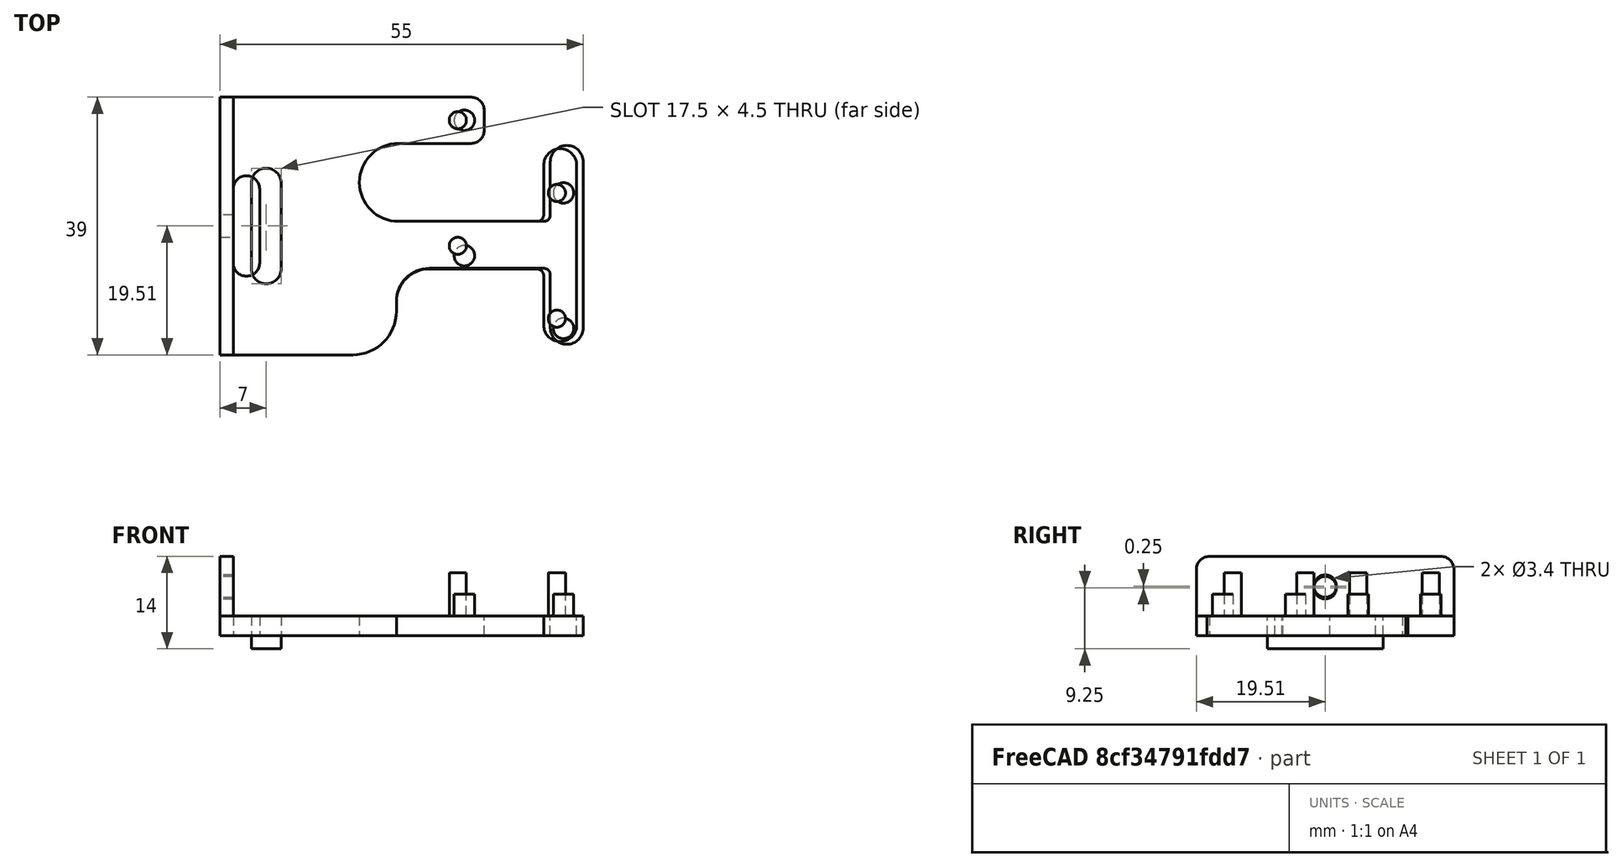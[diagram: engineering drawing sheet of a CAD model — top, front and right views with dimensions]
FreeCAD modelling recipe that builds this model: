
FCSTD DOCUMENT  (FreeCAD 0.15R4649 (Git))
Label: renacuajo-snifferV3
License: CC-BY 3.0
LicenseURL: http://creativecommons.org/licenses/by/3.0/
objects: Sketcher::SketchObject×5, PartDesign::Pad×3, PartDesign::Pocket×2, Part::Feature×1, Part::MultiFuse×1, Mesh::Feature×1, Part::Fillet×1
note: 18 computed .brp shape members not serialized (recipe doc carries the construction recipe); baked Part::Feature solids carry a one-line shape summary decoded from their .brp

FEATURE [Sketcher::SketchObject] Sketch  label="sniffer-base-sketch"
  sketch-geometry (20):
    g0: LineSegment StartX=-27 StartY=-19.5085 StartZ=0 EndX=-27 EndY=19.4915 EndZ=0
    g1: LineSegment StartX=-27 StartY=19.4915 StartZ=0 EndX=11 EndY=19.4915 EndZ=0
    g2: LineSegment StartX=13 StartY=17.4915 StartZ=0 EndX=13 EndY=14.4915 EndZ=0
    g3: LineSegment StartX=11 StartY=12.4915 StartZ=0 EndX=0 EndY=12.4915 EndZ=0
    g4: LineSegment StartX=-27 StartY=-19.5085 StartZ=0 EndX=-6.9 EndY=-19.5085 EndZ=0
    g5: LineSegment StartX=-0.3 StartY=-12.9085 StartZ=0 EndX=-0.3 EndY=-11.4085 EndZ=0
    g6: LineSegment StartX=4.7 StartY=-6.4085 StartZ=0 EndX=22 EndY=-6.4085 EndZ=0
    g7: LineSegment StartX=23 StartY=-7.4085 StartZ=0 EndX=23 EndY=-15.4085 EndZ=0
    g8: LineSegment StartX=28 StartY=-15.4085 StartZ=0 EndX=28 EndY=9.6915 EndZ=0
    g9: LineSegment StartX=23 StartY=9.69149 StartZ=0 EndX=23 EndY=1.69149 EndZ=0
    g10: LineSegment StartX=22 StartY=0.691495 StartZ=0 EndX=-3.5568e-08 EndY=0.691495 EndZ=0
    g11: ArcOfCircle CenterX=-9.4139e-08 CenterY=6.5915 CenterZ=0 NormalX=0 NormalY=0 NormalZ=1 Radius=5.9 StartAngle=1.5708 EndAngle=4.71239
    g12: ArcOfCircle CenterX=11 CenterY=17.4915 CenterZ=0 NormalX=0 NormalY=0 NormalZ=1 Radius=2 StartAngle=0 EndAngle=1.5708
    g13: ArcOfCircle CenterX=11 CenterY=14.4915 CenterZ=0 NormalX=0 NormalY=0 NormalZ=1 Radius=2 StartAngle=4.71239 EndAngle=6.28319
    g14: ArcOfCircle CenterX=-6.9 CenterY=-12.9085 CenterZ=0 NormalX=0 NormalY=0 NormalZ=1 Radius=6.6 StartAngle=4.71239 EndAngle=6.28319
    g15: ArcOfCircle CenterX=4.7 CenterY=-11.4085 CenterZ=0 NormalX=0 NormalY=0 NormalZ=1 Radius=5 StartAngle=1.5708 EndAngle=3.14159
    g16: ArcOfCircle CenterX=22 CenterY=-7.4085 CenterZ=0 NormalX=0 NormalY=0 NormalZ=1 Radius=1 StartAngle=0 EndAngle=1.5708
    g17: ArcOfCircle CenterX=25.5 CenterY=-15.4085 CenterZ=0 NormalX=0 NormalY=0 NormalZ=1 Radius=2.5 StartAngle=3.1416 EndAngle=6.28319
    g18: ArcOfCircle CenterX=22 CenterY=1.69149 CenterZ=0 NormalX=0 NormalY=0 NormalZ=1 Radius=1 StartAngle=4.71239 EndAngle=6.28319
    g19: ArcOfCircle CenterX=25.5 CenterY=9.6915 CenterZ=0 NormalX=0 NormalY=0 NormalZ=1 Radius=2.5 StartAngle=1.3074e-08 EndAngle=3.14159
  constraints (57):
    c: Vertical(g0)
    c: Coincident(g0,g1)
    c: Horizontal(g1)
    c: Vertical(g2)
    c: Horizontal(g3)
    c: Horizontal(g4)
    c: Horizontal(g6)
    c: Vertical(g7)
    c: Vertical(g8)
    c: Vertical(g9)
    c: Horizontal(g10)
    c: Coincident(g4,g0)
    c: Vertical(g5)
    c: PointOnObject(g11,g-2)
    c: Coincident(g11,g3)
    c: Coincident(g11,g10)
    c: Tangent(g11,g3)
    c: Tangent(g10,g11)
    c: Tangent(g1,g12)
    c: Tangent(g2,g12)
    c: Tangent(g2,g13)
    c: Tangent(g3,g13)
    c: Radius(g12) = 2
    c: Equal(g13,g12)
    c: DistanceY(g1,g3) = -7
    c: DistanceX(g0,g2) = 40
    c: DistanceY(g0) = 39
    c: DistanceY(g3,g10) = -11.8
    c: DistanceX(g0) = -27
    c: DistanceY(g0) = 19.4915
    c: Tangent(g4,g14)
    c: Tangent(g5,g14)
    c: Tangent(g5,g15)
    c: Tangent(g6,g15)
    c: DistanceX(g0,g5) = 26.7
    c: Radius(g14) = 6.6
    c: Radius(g15) = 5
    c: DistanceY(g5) = 1.5
    c: Tangent(g6,g16)
    c: Tangent(g7,g16)
    c: DistanceX(g7,g5) = -23.3
    c: Radius(g16) = 1
    c: Coincident(g17,g7)
    c: Coincident(g17,g8)
    c: Tangent(g7,g17)
    c: Tangent(g17,g8)
    c: DistanceY(g7) = -8
    c: Tangent(g9,g18)
    c: Tangent(g10,g18)
    c: Equal(g16,g18)
    c: Equal(g7,g9)
    c: Coincident(g19,g8)
    c: Coincident(g19,g9)
    c: Tangent(g19,g8)
    c: Tangent(g19,g9)
    c: Equal(g19,g17)
    c: DistanceX(g7,g8) = 5
FEATURE [PartDesign::Pad] Pad  label="sniffer-base"
  Length = 3
  Length2 = 100
  Sketch = -> Sketch
  Type = 0
FEATURE [Sketcher::SketchObject] Sketch001  label="vertical-wall-sketch"
  ExternalGeometry = -> [Pad]
  Placement = pos=(-27,0,0) rot=(0.57735,-0.57735,-0.57735;2.0944rad)
  Support = -> Pad [Face2]
  sketch-geometry (6):
    g0: LineSegment StartX=-17.4915 StartY=12 StartZ=0 EndX=17.5085 EndY=12 EndZ=0
    g1: LineSegment StartX=19.5085 StartY=10 StartZ=0 EndX=19.5085 EndY=0 EndZ=0
    g2: LineSegment StartX=19.5085 StartY=0 StartZ=0 EndX=-19.4915 EndY=0 EndZ=0
    g3: LineSegment StartX=-19.4915 StartY=0 StartZ=0 EndX=-19.4915 EndY=10 EndZ=0
    g4: ArcOfCircle CenterX=-17.4915 CenterY=10 CenterZ=0 NormalX=0 NormalY=0 NormalZ=1 Radius=2 StartAngle=1.5708 EndAngle=3.14159
    g5: ArcOfCircle CenterX=17.5085 CenterY=10 CenterZ=0 NormalX=0 NormalY=0 NormalZ=1 Radius=2 StartAngle=0 EndAngle=1.5708
  constraints (15):
    c: Coincident(g1,g2)
    c: Coincident(g2,g3)
    c: Horizontal(g0)
    c: Horizontal(g2)
    c: Vertical(g1)
    c: Vertical(g3)
    c: Coincident(g2,g-3)
    c: Coincident(g1,g-3)
    c: Tangent(g0,g4)
    c: Tangent(g3,g4)
    c: Tangent(g0,g5)
    c: Tangent(g1,g5)
    c: DistanceY(g2,g0) = 12
    c: Radius(g4) = 2
    c: Equal(g5,g4)
FEATURE [PartDesign::Pad] Pad001  label="vertical-wall"
  Length = 2
  Length2 = 100
  Reversed = true
  Sketch = -> Sketch001
  Type = 0
FEATURE [Sketcher::SketchObject] Sketch003  label="poles-sketch"
  Placement = pos=(0,0,3) rot=(0,0,1;0rad)
  sketch-geometry (9):
    g0: Circle CenterX=10 CenterY=16 CenterZ=0 NormalX=0 NormalY=0 NormalZ=1 Radius=1.55
    g1: Circle CenterX=25 CenterY=5 CenterZ=0 NormalX=0 NormalY=0 NormalZ=1 Radius=1.55
    g2: Circle CenterX=10 CenterY=-4.5 CenterZ=0 NormalX=0 NormalY=0 NormalZ=1 Radius=1.55
    g3: Circle CenterX=25 CenterY=-15.5 CenterZ=0 NormalX=0 NormalY=0 NormalZ=1 Radius=1.55
    g4: LineSegment [constr] StartX=10 StartY=16 StartZ=0 EndX=10 EndY=-4.5 EndZ=0
    g5: LineSegment [constr] StartX=10 StartY=16 StartZ=0 EndX=25 EndY=16 EndZ=0
    g6: LineSegment [constr] StartX=25 StartY=16 StartZ=0 EndX=25 EndY=5 EndZ=0
    g7: LineSegment [constr] StartX=10 StartY=-4.5 StartZ=0 EndX=25 EndY=-4.5 EndZ=0
    g8: LineSegment [constr] StartX=25 StartY=-4.5 StartZ=0 EndX=25 EndY=-15.5 EndZ=0
  constraints (24):
    c: Radius(g0) = 1.55
    c: Equal(g0,g1)
    c: Equal(g1,g2)
    c: Equal(g2,g3)
    c: DistanceX(g0,g1) = 15
    c: DistanceY(g0,g1) = -11
    c: Vertical(g4)
    c: Coincident(g4,g0)
    c: Coincident(g4,g2)
    c: DistanceX(g0) = 10
    c: DistanceY(g0) = 16
    c: Horizontal(g5)
    c: Vertical(g6)
    c: Coincident(g6,g5)
    c: Coincident(g5,g0)
    c: Coincident(g6,g1)
    c: Horizontal(g7)
    c: Vertical(g8)
    c: Coincident(g7,g8)
    c: Coincident(g7,g2)
    c: DistanceY(g4) = -20.5
    c: Equal(g7,g5)
    c: Equal(g8,g6)
    c: Coincident(g3,g8)
FEATURE [PartDesign::Pad] Pad002  label="poles"
  Length = 3.25
  Length2 = 100
  Placement = pos=(0,0,3) rot=(0,0,1;0rad)
  Sketch = -> Sketch003
  Type = 0
FEATURE [Part::Feature] Pocket001001  label="renacuajo-sniffer"
  shape: bbox 54 x 39 x 12 mm, 38 faces (baked)
FEATURE [Sketcher::SketchObject] Sketch006  label="boceto_slot"
  Placement = pos=(0,0,3) rot=(0,0,1;0rad)
  Support = -> Pad001 [Face3]
  sketch-geometry (4):
    g0: ArcOfCircle CenterX=-20 CenterY=6.5 CenterZ=0 NormalX=0 NormalY=0 NormalZ=1 Radius=2.25 StartAngle=0 EndAngle=3.14159
    g1: ArcOfCircle CenterX=-20 CenterY=-6.5 CenterZ=0 NormalX=0 NormalY=0 NormalZ=1 Radius=2.25 StartAngle=3.14159 EndAngle=6.28319
    g2: LineSegment StartX=-22.25 StartY=6.5 StartZ=0 EndX=-22.25 EndY=-6.5 EndZ=0
    g3: LineSegment StartX=-17.75 StartY=6.5 StartZ=0 EndX=-17.75 EndY=-6.5 EndZ=0
  constraints (10):
    c: Tangent(g0,g3) = 1.5708
    c: Tangent(g0,g2) = -1.5708
    c: Tangent(g2,g1) = -1.5708
    c: Tangent(g3,g1) = 1.5708
    c: Vertical(g2)
    c: Equal(g0,g1)
    c: Radius(g0) = 2.25
    c: DistanceY(g0,g1) = -13
    c: Symmetric(g1,g0,g-1)
    c: DistanceX(g-1,g0) = -20
FEATURE [PartDesign::Pocket] Pocket  label="slot"
  Length = 5
  Sketch = -> Sketch006
  Type = 0
FEATURE [Sketcher::SketchObject] Sketch007  label="drill-sketch"
  ExternalGeometry = -> [Pocket]
  Placement = pos=(-27,0,0) rot=(0.57735,-0.57735,-0.57735;2.0944rad)
  Support = -> Pocket [Face9]
  sketch-geometry (1):
    g0: Circle CenterX=0 CenterY=7.25 CenterZ=0 NormalX=0 NormalY=0 NormalZ=1 Radius=1.7
  constraints (3):
    c: PointOnObject(g0,g-2)
    c: Radius(g0) = 1.7
    c: DistanceY(g-1,g0) = 7.25
FEATURE [PartDesign::Pocket] Pocket001002  label="drill"
  Length = 5
  Sketch = -> Sketch007
  Type = 0
FEATURE [Part::MultiFuse] Fusion  label="sniffer-union"
  Shapes = -> [Pad002,Pocket001002]
FEATURE [Mesh::Feature] Slineas
FEATURE [Part::Fillet] Fillet  label="sniffer"
  Base = -> Fusion
  Edges = 4 edges r=0.3: [Edge54,Edge55,Edge56,Edge61]
